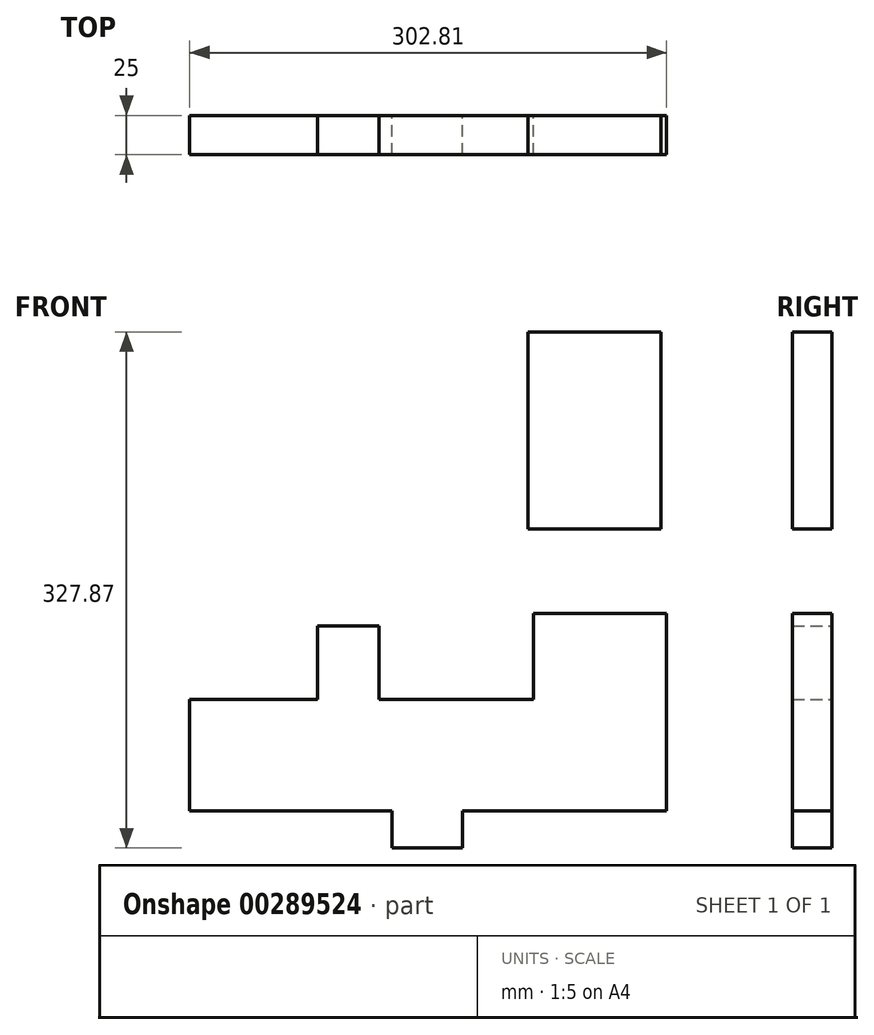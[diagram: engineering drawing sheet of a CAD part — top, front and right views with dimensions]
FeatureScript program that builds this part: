
annotation { "Feature Type Name" : "Feature", "Feature Type Description" : "" }
export const myFeature = defineFeature(function(context is Context, id is Id, definition is map)
    precondition{}
    {
        {
            var Q0;
            Q0=qCreatedBy(makeId("Front.planeOp"),FACE);
            var sketch = newSketch(context, id + "F0", { "sketchPlane" : qUnion([Q0])});
            skLineSegment(sketch, "E0.bottom", {"start": v(-82.71, 179.43) * mm, "end": v(-167.18, 179.43) * mm});
            skLineSegment(sketch, "E0.top", {"start": v(-82.71, 53.97) * mm, "end": v(-212.13, 53.97) * mm});
            skLineSegment(sketch, "E0.left", {"start": v(-82.71, 179.43) * mm, "end": v(-82.71, 53.97) * mm});
            skLineSegment(sketch, "E0.right", {"start": v(-385.52, 124.6) * mm, "end": v(-385.52, 53.97) * mm});
            skLineSegment(sketch, "E1.bottom", {"start": v(-385.52, 53.97) * mm, "end": v(-321.3, 53.97) * mm});
            skLineSegment(sketch, "E1.top", {"start": v(-385.52, 124.6) * mm, "end": v(-321.3, 124.6) * mm});
            skLineSegment(sketch, "E1.left", {"start": v(-385.52, 53.97) * mm, "end": v(-385.52, 124.6) * mm});
            skLineSegment(sketch, "E1.right", {"start": v(-321.3, 53.97) * mm, "end": v(-321.3, 124.6) * mm});
            skLineSegment(sketch, "E2.bottom", {"start": v(-321.3, 53.97) * mm, "end": v(-284.25, 53.97) * mm});
            skLineSegment(sketch, "E2.top", {"start": v(-321.3, 76.2) * mm, "end": v(-284.25, 76.2) * mm});
            skLineSegment(sketch, "E2.left", {"start": v(-321.3, 53.97) * mm, "end": v(-321.3, 76.2) * mm});
            skLineSegment(sketch, "E2.right", {"start": v(-284.25, 53.97) * mm, "end": v(-284.25, 76.2) * mm});
            skLineSegment(sketch, "E3.bottom", {"start": v(-284.25, 53.97) * mm, "end": v(-257.09, 53.97) * mm});
            skLineSegment(sketch, "E3.top", {"start": v(-284.25, 76.2) * mm, "end": v(-257.09, 76.2) * mm});
            skLineSegment(sketch, "E3.right", {"start": v(-257.09, 53.97) * mm, "end": v(-257.09, 76.2) * mm});
            skLineSegment(sketch, "E4.bottom", {"start": v(-82.71, 53.97) * mm, "end": v(-167.18, 53.97) * mm});
            skLineSegment(sketch, "E4.top", {"start": v(-82.71, 106.33) * mm, "end": v(-167.18, 106.33) * mm});
            skLineSegment(sketch, "E4.left", {"start": v(-82.71, 53.97) * mm, "end": v(-82.71, 106.33) * mm});
            skLineSegment(sketch, "E4.right", {"start": v(-167.18, 53.97) * mm, "end": v(-167.18, 106.33) * mm});
            skLineSegment(sketch, "E5.bottom", {"start": v(-321.3, 124.6) * mm, "end": v(-82.71, 124.6) * mm});
            skLineSegment(sketch, "E5.top", {"start": v(-321.3, 124.6) * mm, "end": v(-82.71, 124.6) * mm});
            skLineSegment(sketch, "E5.left", {"start": v(-321.3, 124.6) * mm, "end": v(-321.3, 124.6) * mm});
            skLineSegment(sketch, "E5.right", {"start": v(-82.71, 124.6) * mm, "end": v(-82.71, 124.6) * mm});
            skLineSegment(sketch, "E6.bottom", {"start": v(-124.95, 106.33) * mm, "end": v(-167.18, 106.33) * mm});
            skLineSegment(sketch, "E6.top", {"start": v(-124.95, 53.97) * mm, "end": v(-167.18, 53.97) * mm});
            skLineSegment(sketch, "E6.left", {"start": v(-124.95, 106.33) * mm, "end": v(-124.95, 53.97) * mm});
            skLineSegment(sketch, "E6.right", {"start": v(-167.18, 106.33) * mm, "end": v(-167.18, 53.97) * mm});
            skLineSegment(sketch, "E7.top", {"start": v(-82.71, 124.6) * mm, "end": v(-167.18, 124.6) * mm});
            skLineSegment(sketch, "E7.left", {"start": v(-82.71, 179.43) * mm, "end": v(-82.71, 124.6) * mm});
            skLineSegment(sketch, "E7.right", {"start": v(-167.18, 179.43) * mm, "end": v(-167.18, 124.6) * mm});
            skLineSegment(sketch, "E8.bottom", {"start": v(-167.18, 106.33) * mm, "end": v(-257.09, 106.33) * mm});
            skLineSegment(sketch, "E8.top", {"start": v(-167.18, 53.97) * mm, "end": v(-212.13, 53.97) * mm});
            skLineSegment(sketch, "E8.right", {"start": v(-257.09, 106.33) * mm, "end": v(-257.09, 53.97) * mm});
            skLineSegment(sketch, "E9.bottom", {"start": v(-212.13, 106.33) * mm, "end": v(-257.09, 106.33) * mm});
            skLineSegment(sketch, "E9.top", {"start": v(-212.13, 30.26) * mm, "end": v(-257.09, 30.26) * mm});
            skLineSegment(sketch, "E9.left", {"start": v(-212.13, 106.33) * mm, "end": v(-212.13, 30.26) * mm});
            skLineSegment(sketch, "E9.right", {"start": v(-257.09, 106.33) * mm, "end": v(-257.09, 30.26) * mm});
            skLineSegment(sketch, "E10.trimOffspring", {"start": v(-257.09, 53.97) * mm, "end": v(-385.52, 53.97) * mm});
            skLineSegment(sketch, "E11.bottom", {"start": v(-385.52, 124.6) * mm, "end": v(-304.41, 124.6) * mm});
            skLineSegment(sketch, "E11.right", {"start": v(-304.41, 124.6) * mm, "end": v(-304.41, 171.5) * mm});
            skLineSegment(sketch, "E12.bottom", {"start": v(-304.41, 171.5) * mm, "end": v(-265.35, 171.5) * mm});
            skLineSegment(sketch, "E12.top", {"start": v(-304.41, 124.6) * mm, "end": v(-265.35, 124.6) * mm});
            skLineSegment(sketch, "E12.left", {"start": v(-304.41, 171.5) * mm, "end": v(-304.41, 124.6) * mm});
            skLineSegment(sketch, "E12.right", {"start": v(-265.35, 171.5) * mm, "end": v(-265.35, 124.6) * mm});
            skLineSegment(sketch, "E13.bottom", {"start": v(-170.8, 358.13) * mm, "end": v(-86.17, 358.13) * mm});
            skLineSegment(sketch, "E13.top", {"start": v(-170.8, 233.04) * mm, "end": v(-86.17, 233.04) * mm});
            skLineSegment(sketch, "E13.left", {"start": v(-170.8, 358.13) * mm, "end": v(-170.8, 233.04) * mm});
            skLineSegment(sketch, "E13.right", {"start": v(-86.17, 358.13) * mm, "end": v(-86.17, 233.04) * mm});
            skLineSegment(sketch, "E14.top", {"start": v(-170.8, 304.68) * mm, "end": v(-86.17, 304.68) * mm});
            skLineSegment(sketch, "E14.left", {"start": v(-170.8, 233.04) * mm, "end": v(-170.8, 304.68) * mm});
            skLineSegment(sketch, "E14.right", {"start": v(-86.17, 233.04) * mm, "end": v(-86.17, 304.68) * mm});
            skLineSegment(sketch, "E15.bottom", {"start": v(-170.8, 358.13) * mm, "end": v(-128.49, 358.13) * mm});
            skLineSegment(sketch, "E15.top", {"start": v(-170.8, 233.04) * mm, "end": v(-128.49, 233.04) * mm});
            skLineSegment(sketch, "E15.right", {"start": v(-128.49, 358.13) * mm, "end": v(-128.49, 304.68) * mm});
            skLineSegment(sketch, "E16.top", {"start": v(-170.8, 286.64) * mm, "end": v(-86.17, 286.64) * mm});
            skLineSegment(sketch, "E16.left", {"start": v(-170.8, 304.68) * mm, "end": v(-170.8, 286.64) * mm});
            skLineSegment(sketch, "E16.right", {"start": v(-86.17, 304.68) * mm, "end": v(-86.17, 286.64) * mm});
            skLineSegment(sketch, "E17.trimOffspring", {"start": v(-128.49, 286.64) * mm, "end": v(-128.49, 233.04) * mm});
            skSolve(sketch);
        }
        {
            var Q0;
            Q0 = qSketchRegion(id + "F0", true);
            extrude(context, id + "F1", {"entities" : qUnion([Q0]), "depth" : 25 * mm});
        }
    });
